# Revit family: PRD_AR_ShwrMxrs_BasicInstallationKitForShower_F3BX2001
name_source: partatom
category: Plumbing Fixtures
revit_build: Autodesk Revit 2018 (Build: 20190510_1515(x64)
units: mm (PartAtom-declared; Revit-internal decimal feet)

## family parameters
Cut with Voids When Loaded = No
Host = Face
OmniClass Number = 23.45.05.14.99
OmniClass Title = Other Sanitary Washing Plumbing Fixtures
Part Type = Normal
Room Calculation Point = No
Round Connector Dimension = Use Diameter
Shared = Yes

## types (1)
- F3BX2001 - with mixing unit
    AssetType = Fixed
    BIMObjectName = PRD_AR_ShowerManualWaterSupplySets_BasicInstallationKitForShower_F3BX2001
    BodyMaterial = Plastic
    Category = Pr_40_20_87_78, Shower manual water supply sets
    CloseOffRating = 0
    Default Elevation = 1000 mm  [stored 3.28084 ft]
    Description = R3 basic installation kit for in-wall mounting of finished installation kits DN 15 with mixing unit, for shower facilities. For connection to hot and cold water. KWC system box made of plastic, 174 x 225 mm, with connection screws, shell protection, flush connector for flushing, and leak test.
    DiameterNominal = 15  [stored 0.0492126 ft]
    DurationUnit = year
    FlowCoefficient = 0
    GrossWeight = 1.20 kg
    IfcExportAs = IfcValveType
    IfcExportType = MIXING
    InstalationKitMaterial = <By Category>
    Manufacturer = KWC Group AG
    ManufacturerName = KWC Group AG
    ManufacturerURL = www.kwc.com
    Material = Plastic
    MaterialsBody = Plastic
    MixerControl = Other
    Model = F3BX2001
    ModelNumber = 2030036141
    ModelReference = F3BX2001
    NBSDescription = Shower mixers
    NBSReference = 45-35-70/335
    Name = F3 Basic installation kit for shower F3BX2001
    NetWeight = 1.14 kg
    NominalHeight = 225 mm  [stored 0.738189 ft]
    NominalLength = 0 mm  [stored 0 ft]
    NominalWidth = 174 mm  [stored 0.570866 ft]
    OutletConnectionSize = 12.7  [stored 0.0416667 ft]
    OverallDepth = 80 mm  [stored 0.262467 ft]
    ProductInformation = https://pim.kwc.com
    Size = 15 mm  [stored 0.0492126 ft]
    TestPressure = 0
    TypeOfMixing = with thermostat / mixer
    TypeOfMounting = In-Wall-Installation-With-Box
    URL = www.kwc.com
    Uniclass2015Code = Pr_40_20_87_78
    Uniclass2015Title = Shower manual water supply sets
    Uniclass2015Version = Products v1.7
    ValveMechanism = Other
    ValveOperation = Other
    Version = 1
    WarrantyDurationUnit = year

note: [stored X ft] marks values corroborated as IEEE doubles in the binary element streams (Revit-internal decimal feet)

## geometry (parser evidence)
native form markers: Sweep x3
no freeform markers — native parametric forms only
